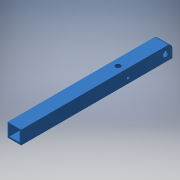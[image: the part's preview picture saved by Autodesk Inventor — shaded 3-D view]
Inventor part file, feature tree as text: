
AUTODESK INVENTOR PART (.ipt)
format: ipt  version: 2017 SP1 (Build 210196100, 196)  size: 134,656 bytes
history: native  units: in
note: dims shown in document units (in); Inventor stores cm internally (conversion verified against a paired STEP export)
features: extrude x3, sketch x3, fillet x1
ambient origin geometry x8: Origin, YZ Plane, XZ Plane, XY Plane, X Axis, Y Axis, Z Axis, Center Point
bodies: Solid1 (feature_tree)
feature tree (7):
  extrude  "Extrusion1"  Depth=0.125in
  extrude  "Extrusion2"  Depth=0.375in
  extrude  "Extrusion3"  Depth=0.375in TaperAngle=0.0deg
  fillet  "Fillet1"  Radius=5.5in
  sketch  "Sketch1"  dims[d0=1.0in d1=0.125in]
  sketch  "Sketch2"  dims[d2=11.125in d3=0.0in d4=0.375in]
  sketch  "Sketch3"  dims[d5=0.5in d6=5.5in d7=0.0in d10=5.5in d11=0.0in d13=0.375in d15=0.125in d19=0.2in d20=2.75in d21=0.125in d22=3.5in d23=0.5in d24=0.375in]
